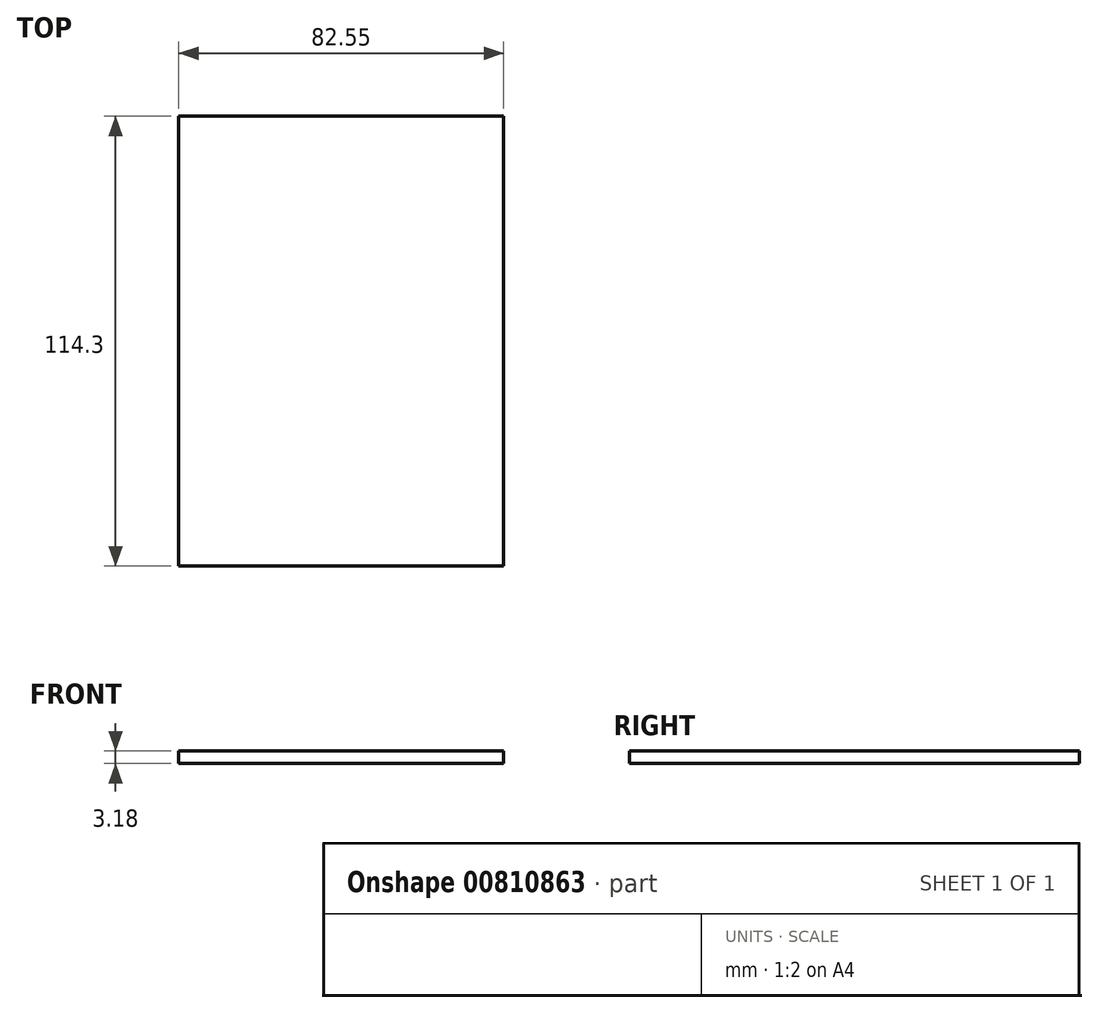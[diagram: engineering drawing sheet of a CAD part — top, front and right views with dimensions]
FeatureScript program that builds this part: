
annotation { "Feature Type Name" : "Feature", "Feature Type Description" : "" }
export const myFeature = defineFeature(function(context is Context, id is Id, definition is map)
    precondition{}
    {
        {
            var Q0;
            Q0=qCreatedBy(makeId("Right.planeOp"),FACE);
            var sketch = newSketch(context, id + "F0", { "sketchPlane" : qUnion([Q0])});
            skLineSegment(sketch, "E0.bottom", {"start": v(-57.15, 1.59) * mm, "end": v(57.15, 1.59) * mm});
            skLineSegment(sketch, "E0.top", {"start": v(-57.15, -1.59) * mm, "end": v(57.15, -1.59) * mm});
            skLineSegment(sketch, "E0.left", {"start": v(-57.15, 1.59) * mm, "end": v(-57.15, -1.59) * mm});
            skLineSegment(sketch, "E0.right", {"start": v(57.15, 1.59) * mm, "end": v(57.15, -1.59) * mm});
            skPoint(sketch, "E0.middle", {"position": v(0, 0) * mm});
            skSolve(sketch);
        }
        {
            var Q0;
            Q0=makeQuery(id+"F0.imprint","IMPRINT",FACE,{"disambiguationData":[TD([[makeQuery(id+"F0.imprint","IMPRINT",EDGE,{"derivedFrom":sQuery(id+"F0.wireOp",EDGE,"E0.bottom")}),-1.0]])]});
            extrude(context, id + "F1", {"entities" : qUnion([Q0]), "depth" : 82.55 * mm, "offsetDistance" : 25.4 * mm});
        }
    });
